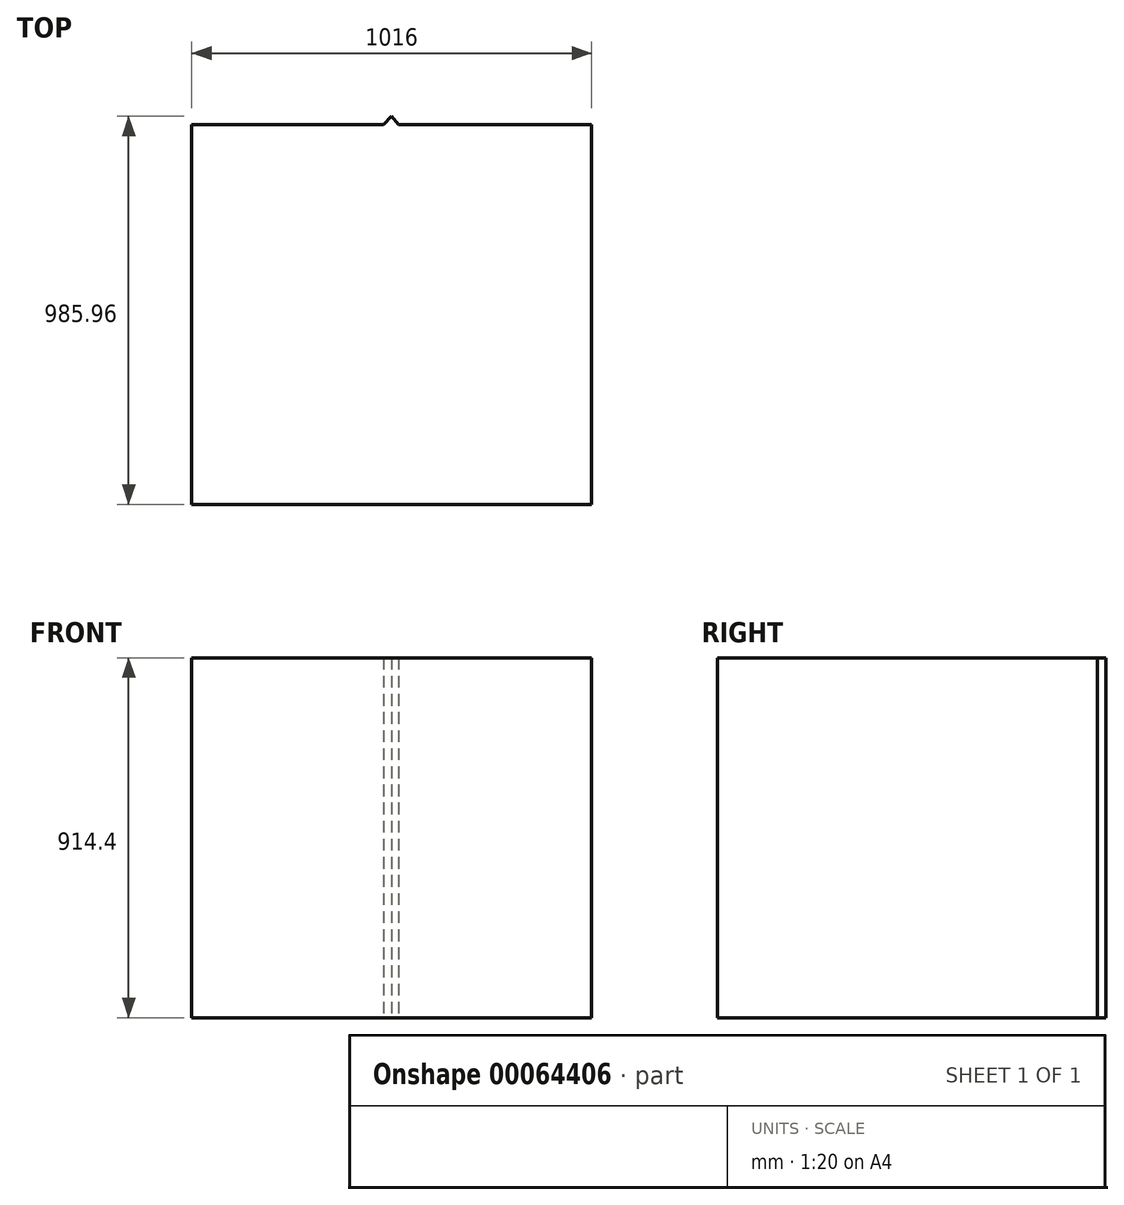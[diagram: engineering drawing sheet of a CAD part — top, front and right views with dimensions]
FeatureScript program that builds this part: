
annotation { "Feature Type Name" : "Feature", "Feature Type Description" : "" }
export const myFeature = defineFeature(function(context is Context, id is Id, definition is map)
    precondition{}
    {
        {
            var Q0;
            Q0=qCreatedBy(makeId("Top.planeOp"),FACE);
            var sketch = newSketch(context, id + "F0", { "sketchPlane" : qUnion([Q0])});
            skLineSegment(sketch, "E0.rect.bottom", {"start": v(-508, 482.6) * mm, "end": v(508, 482.6) * mm});
            skLineSegment(sketch, "E0.rect.top", {"start": v(-508, -482.6) * mm, "end": v(508, -482.6) * mm});
            skLineSegment(sketch, "E0.rect.left", {"start": v(-508, 482.6) * mm, "end": v(-508, -482.6) * mm});
            skLineSegment(sketch, "E0.rect.right", {"start": v(508, 482.6) * mm, "end": v(508, -482.6) * mm});
            skPoint(sketch, "E0.rect.middle", {"position": v(0, 0) * mm});
            skLineSegment(sketch, "E1", {"start": v(0, 482.6) * mm, "end": v(0, 503.36) * mm});
            skPoint(sketch, "E1.endSnap0", {"position": v(0, 482.6) * mm});
            skLineSegment(sketch, "E2", {"start": v(0, 503.36) * mm, "end": v(0, 482.6) * mm});
            skLineSegment(sketch, "E3", {"start": v(0, 503.36) * mm, "end": v(17.44, 482.6) * mm});
            skLineSegment(sketch, "E4", {"start": v(17.44, 482.6) * mm, "end": v(-21.32, 482.6) * mm});
            skLineSegment(sketch, "E5", {"start": v(-21.32, 482.6) * mm, "end": v(0, 503.36) * mm});
            skSolve(sketch);
        }
        {
            var Q0;
            Q0 = qSketchRegion(id + "F0", true);
            extrude(context, id + "F1", {"entities" : qUnion([Q0]), "depth" : 914.4 * mm});
        }
    });
